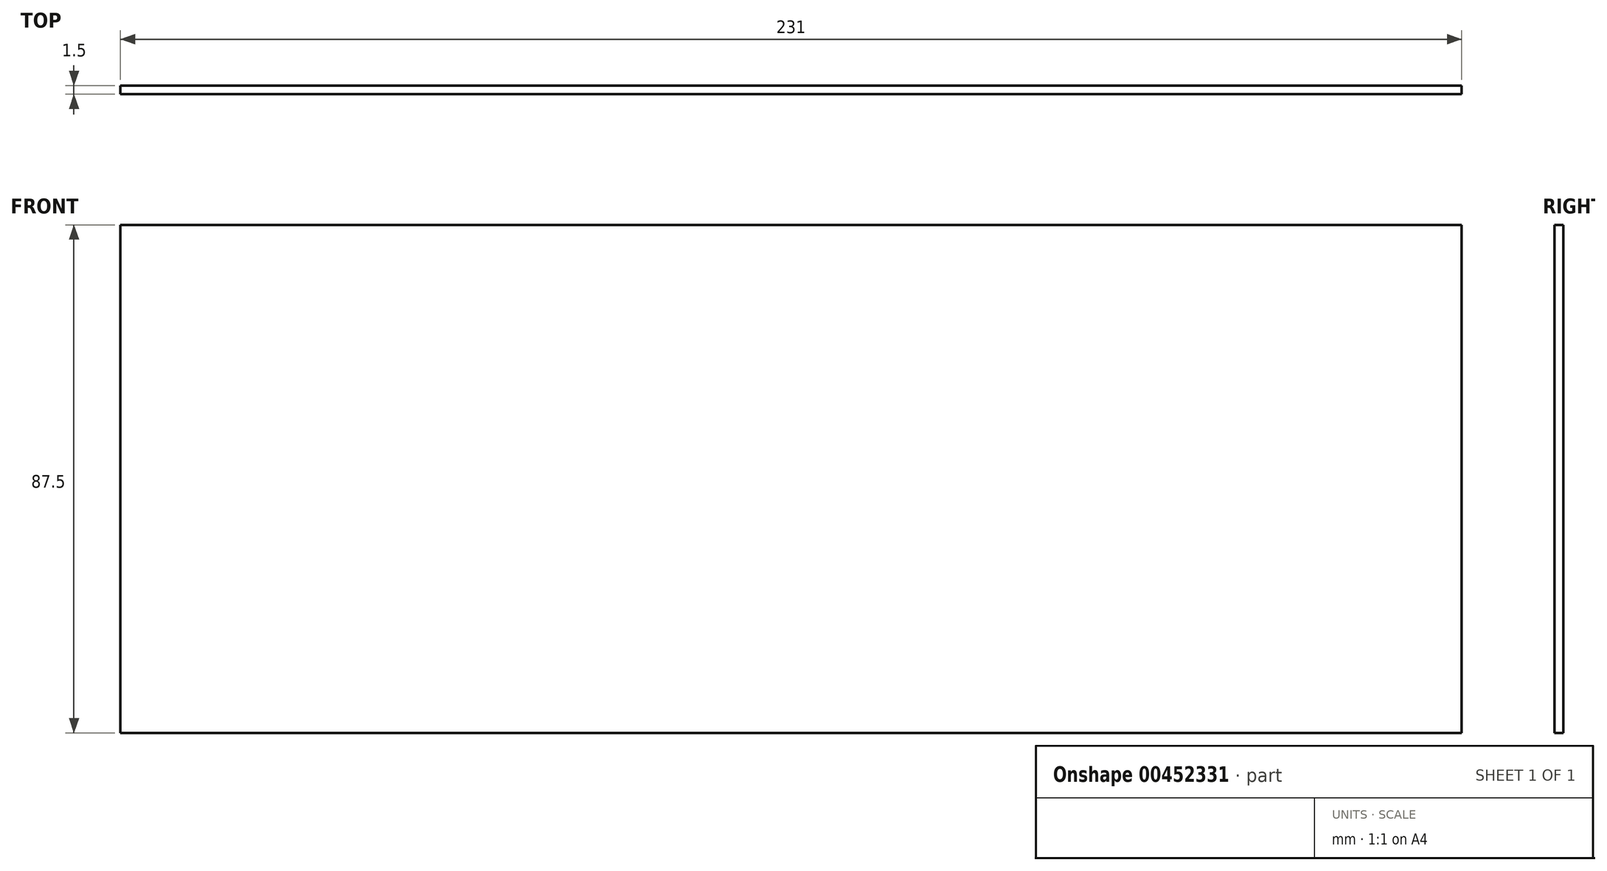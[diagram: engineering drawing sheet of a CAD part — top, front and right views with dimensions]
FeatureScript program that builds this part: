
annotation { "Feature Type Name" : "Feature", "Feature Type Description" : "" }
export const myFeature = defineFeature(function(context is Context, id is Id, definition is map)
    precondition{}
    {
        {
            var Q0;
            Q0=qCreatedBy(makeId("Front.planeOp"),FACE);
            var sketch = newSketch(context, id + "F0", { "sketchPlane" : qUnion([Q0])});
            skLineSegment(sketch, "E0.bottom", {"start": v(-79.93, -38.82) * mm, "end": v(151.07, -38.82) * mm});
            skLineSegment(sketch, "E0.top", {"start": v(-79.93, 48.68) * mm, "end": v(151.07, 48.68) * mm});
            skLineSegment(sketch, "E0.left", {"start": v(-79.93, -38.82) * mm, "end": v(-79.93, 48.68) * mm});
            skLineSegment(sketch, "E0.right", {"start": v(151.07, -38.82) * mm, "end": v(151.07, 48.68) * mm});
            skSolve(sketch);
        }
        {
            var Q0;
            Q0 = qSketchRegion(id + "F0", true);
            extrude(context, id + "F1", {"entities" : qUnion([Q0]), "depth" : 1.5 * mm});
        }
    });
